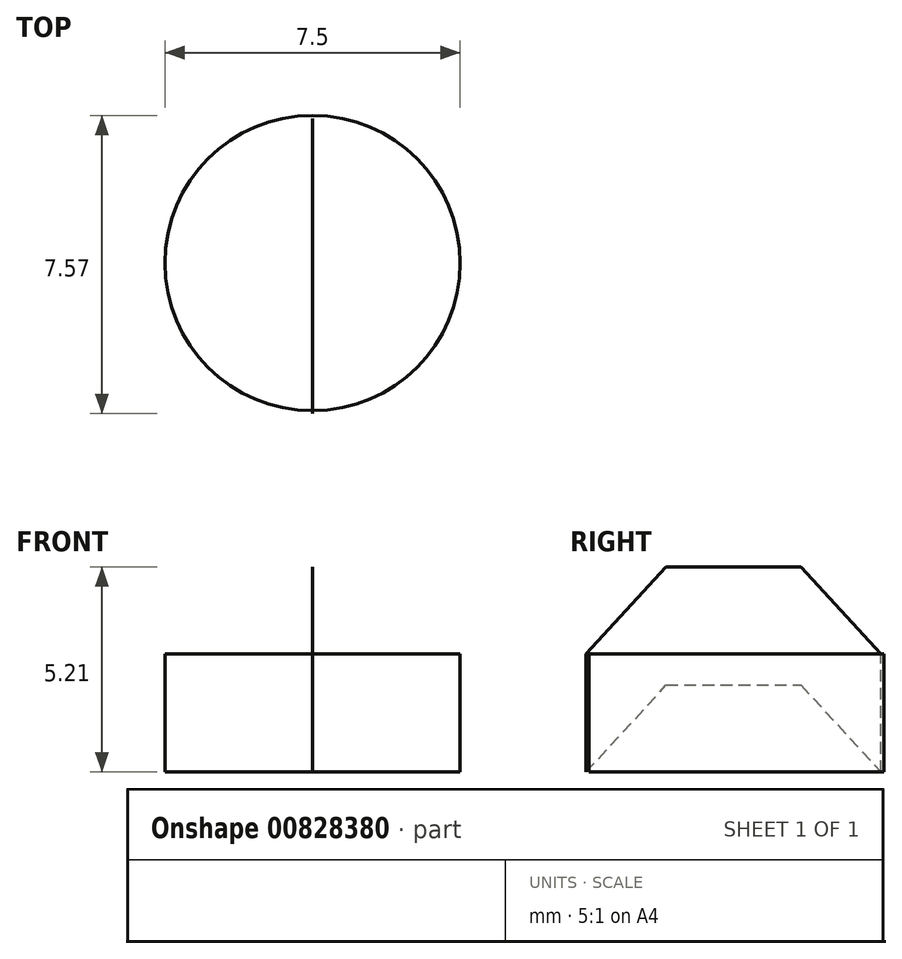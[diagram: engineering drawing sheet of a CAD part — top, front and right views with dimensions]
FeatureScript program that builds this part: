
annotation { "Feature Type Name" : "Feature", "Feature Type Description" : "" }
export const myFeature = defineFeature(function(context is Context, id is Id, definition is map)
    precondition{}
    {
        {
            var Q0;
            Q0=qCreatedBy(makeId("Right.planeOp"),FACE);
            var sketch = newSketch(context, id + "F0", { "sketchPlane" : qUnion([Q0])});
            skLineSegment(sketch, "E0", {"start": v(-3.82, 0) * mm, "end": v(-1.79, 2.2) * mm});
            skLineSegment(sketch, "E1", {"start": v(-1.79, 2.2) * mm, "end": v(1.64, 2.2) * mm});
            skLineSegment(sketch, "E2", {"start": v(1.64, 2.2) * mm, "end": v(3.67, 0) * mm});
            skSolve(sketch);
        }
        {
            var Q0;
            Q0=qCreatedBy(makeId("Top.planeOp"),FACE);
            var sketch = newSketch(context, id + "F1", { "sketchPlane" : qUnion([Q0])});
            skCircle(sketch, "E3", {"center": v(0, 0) * mm, "radius": 3.75 * mm});
            skSolve(sketch);
        }
        {
            var Q0;
            Q0=qCreatedBy(makeId("Top.planeOp"),FACE);
            cPlane(context, id + "F2", {"entities" : qUnion([Q0]), "cplaneType" : CPlaneType.OFFSET, "offset" : 2.2 * mm, "width" : 150 * mm, "height" : 150 * mm});
        }
        {
            var Q0;
            Q0=sQuery(id+"F1.wireOp",EDGE,"E3");
            var Q1;
            Q1=sQuery(id+"F0.wireOp",EDGE,"E2");
            var Q2;
            Q2=sQuery(id+"F0.wireOp",EDGE,"E0");
            var Q3;
            Q3=sQuery(id+"F0.wireOp",EDGE,"E1");
            extrude(context, id + "F3", {"bodyType" : ToolBodyType.SURFACE, "surfaceEntities" : qUnion([Q0, Q1, Q2, Q3]), "depth" : 3 * mm, "offsetDistance" : 25 * mm});
        }
    });
